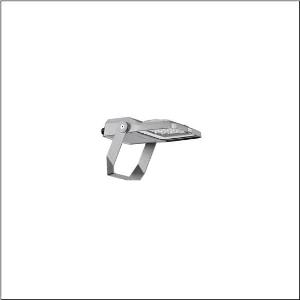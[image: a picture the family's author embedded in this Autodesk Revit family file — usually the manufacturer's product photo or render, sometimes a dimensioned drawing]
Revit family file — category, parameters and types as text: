
# Revit family: floodlight_fl_21_iq_micro___rs12_5xa7761a4b1a_38e5
name_source: partatom
category: Lighting Fixtures
units: mm (PartAtom-declared; Revit-internal decimal feet)

## family parameters
Cut with Voids When Loaded = No
Host = Face
Light Source = No
Part Type = Normal
Room Calculation Point = No
Round Connector Dimension = Use Diameter
Shared = No

## types (1)
- --- (1 x LED, 3220 lm, 23.1 W, 4000K)
    Apparent Load = 23 VA
    CIE Flux Codes = 79 92 99 100 100
    Color Rendering = 70
    Color Temperature = 4000K
    Default Elevation = 1800 mm
    Description = Floodlight FL 21 iQ micro, floodlight, primary light control with lens, of PMMA, primary optical cover: protective disc, of toughened safety glass, transparent, light distribution: RS12, light emission: direct distribution, installation type: surface-mounted, LED, High Power LED, rated luminous flux: 3.220lm, luminous efficacy: 139lm/W, light colour: 740, colour temperature: 4000K, control: optimised constant luminous flux control (CLO 2.0), Desk-Remote (wireless, voltage-free reading and setting of iQ features in the workshop via application-optimized NFC function/RFID function), Light-Fading, Smart-Wire, Night-Set, Lumen-Switch, Temp-Guard, Auto-Match, with terminal, 6-pole, mains connection: 220..240V, AC, 50/60Hz, start of lifetime: 23W, end of service life: 24W, reduction: 11W, luminaire housing, of diecast aluminium, powder-coated, Siteco® metallic grey (DB 702S), corrosivity category C5 mid according to DIN EN ISO 12944, sealing non-destructively replaceable, mounting bracket, of steel, galvanised, powder-coated, Siteco® metallic grey (DB 702S), protection rating (complete): IP66, insulation class (complete): insulation class II (safety insulation), certification: CE, ENEC, VDE, protection symbol: D, impact resistance: IK07, permissible operating ambient temperature: -40..+40°C, permissible operating ambient temperature for outdoor applications: -40..+50°C, standard: DIN EN 12944, LABS conformity tested according to VDMA 24364:2018-05, packaging unit: 1 piece

Light Distribution: RS12
    Height = 65 mm
    Lamp = 1 x LED
    Lamp Light Flux = 3220 lm
    Lamp Power = 23.1 W
    Lamp count = 1
    Length = 312 mm
    Luminous efficacy = 139 lm/W
    Manufacturer = Siteco
    ModVariant = No
    Model = 5XA7761A4B1A
    Mounting Place = Wall
    Mounting Type = Surface mounted
    Number of Poles = 1
    OnlyDefault = Yes
    Power Factor = 1
    Product Name = Floodlight FL 21 iQ micro | RS12
    Product group = floodlight | wall mounted
    ProductGroupID = 2001
    Protection Class = Protection class II
    Protection Degree = IP 66
    RLX_Detail_Level = 1
    RLX_Emergency_Light_Flux = 0 lm
    RLX_Emergency_Type = 0
    RLX_Emergency_Type_DB = No
    RlxData = <blob elided: 74849 chars, md5=b7288f37>
    Socket = socket
    Standby Power = 0 W
    System Light Flux = 3220 lm
    System Power = 23 W
    Type Comments = factory setting: luminous flux: 100 % | dim-lin: 254 | 455 mA
    Type Image = l_1006880.jpg
    URL = http://relux.com
    VarID = @adj_115009
    Voltage = 0 V
    Weight = 0.00 kg
    Width = 230 mm

## geometry (parser evidence)
native form markers: Blend x4, Sweep x12
no freeform markers — native parametric forms only
